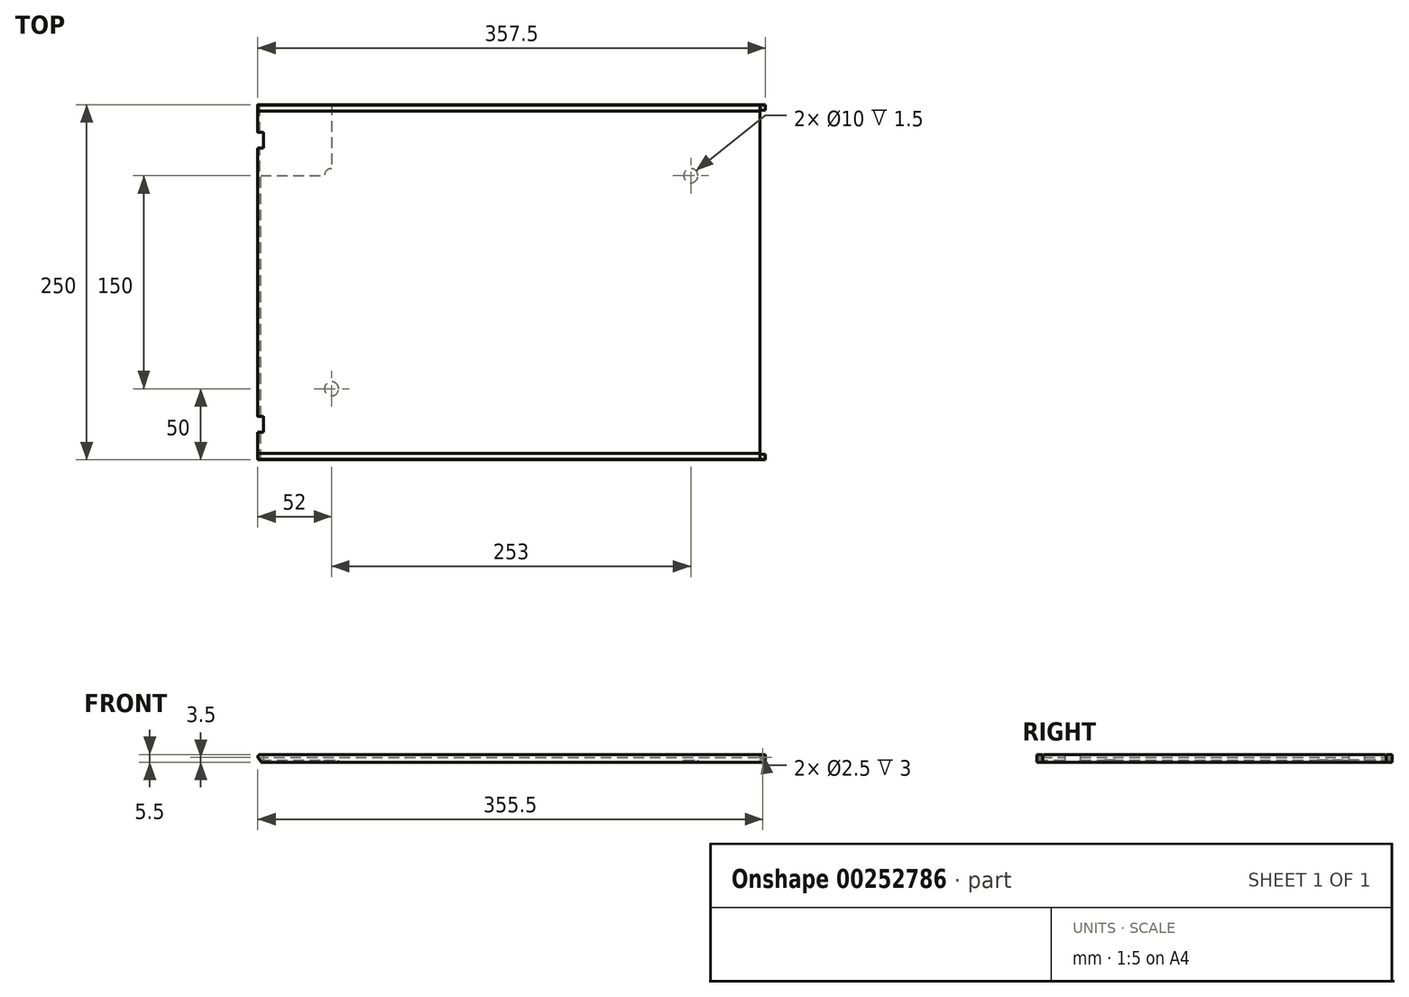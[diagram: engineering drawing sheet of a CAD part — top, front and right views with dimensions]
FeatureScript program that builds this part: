
annotation { "Feature Type Name" : "Feature", "Feature Type Description" : "" }
export const myFeature = defineFeature(function(context is Context, id is Id, definition is map)
    precondition{}
    {
        {
            var Q0;
            Q0=qCreatedBy(makeId("Top.planeOp"),FACE);
            var sketch = newSketch(context, id + "F0", { "sketchPlane" : qUnion([Q0])});
            skLineSegment(sketch, "E0.bottom", {"start": v(-175, -125) * mm, "end": v(175, -125) * mm});
            skLineSegment(sketch, "E0.top", {"start": v(-175, 125) * mm, "end": v(175, 125) * mm});
            skLineSegment(sketch, "E0.left", {"start": v(-175, -125) * mm, "end": v(-175, 125) * mm});
            skLineSegment(sketch, "E0.right", {"start": v(175, -125) * mm, "end": v(175, 125) * mm});
            skPoint(sketch, "E0.middle", {"position": v(0, 0) * mm});
            skSolve(sketch);
        }
        {
            var Q0;
            Q0 = qSketchRegion(id + "F0", true);
            extrude(context, id + "F1", {"entities" : qUnion([Q0]), "endBound" : BoundingType.SYMMETRIC, "depth" : 4 * mm});
        }
        {
            var Q0;
            Q0=makeQuery(id+"F1.opExtrude","SWEPT_FACE",FACE,{"disambiguationData":[OSD([sQuery(id+"F0.wireOp",EDGE,"E0.right")])]});
            var sketch = newSketch(context, id + "F2", { "sketchPlane" : qUnion([Q0])});
            skLineSegment(sketch, "E1.bottom", {"start": v(-125, 2) * mm, "end": v(-121, 2) * mm});
            skLineSegment(sketch, "E1.top", {"start": v(-125, -2) * mm, "end": v(-121, -2) * mm});
            skLineSegment(sketch, "E1.left", {"start": v(-125, 2) * mm, "end": v(-125, -2) * mm});
            skLineSegment(sketch, "E1.right", {"start": v(-121, 2) * mm, "end": v(-121, -2) * mm});
            skLineSegment(sketch, "E2.MirrorCS", {"start": v(125, 2) * mm, "end": v(121, 2) * mm});
            skLineSegment(sketch, "E3.MirrorCS", {"start": v(125, 2) * mm, "end": v(125, -2) * mm});
            skLineSegment(sketch, "E4.MirrorCS", {"start": v(125, -2) * mm, "end": v(121, -2) * mm});
            skLineSegment(sketch, "E5.MirrorCS", {"start": v(121, 2) * mm, "end": v(121, -2) * mm});
            skSolve(sketch);
        }
        {
            var Q0;
            Q0=makeQuery(id+"F2.imprint","IMPRINT",FACE,{"disambiguationData":[TD([[makeQuery(id+"F2.imprint","IMPRINT",EDGE,{"derivedFrom":sQuery(id+"F2.wireOp",EDGE,"E1.bottom")}),-1.0]])]});
            var Q1;
            Q1=makeQuery(id+"F2.imprint","IMPRINT",FACE,{"disambiguationData":[TD([[makeQuery(id+"F2.imprint","IMPRINT",EDGE,{"derivedFrom":sQuery(id+"F2.wireOp",EDGE,"E2.MirrorCS")}),-1.0]])]});
            extrude(context, id + "F3", {"entities" : qUnion([Q0, Q1]), "operationType" : NewBodyOperationType.ADD, "depth" : 4 * mm});
        }
        {
            var Q0;
            Q0=makeQuery(id+"F3.opExtrude","SWEPT_FACE",FACE,{"disambiguationData":[OSD([sQuery(id+"F2.wireOp",EDGE,"E1.right")])]});
            var sketch = newSketch(context, id + "F4", { "sketchPlane" : qUnion([Q0])});
            skCircle(sketch, "E6", {"center": v(-177, 0) * mm, "radius": 1.25 * mm});
            skPoint(sketch, "E6.centerSnap0", {"position": v(-179, 0) * mm});
            skPoint(sketch, "E6.centerSnap1", {"position": v(-177, -2) * mm});
            skSolve(sketch);
        }
        {
            var Q0;
            Q0 = qSketchRegion(id + "F4", true);
            extrude(context, id + "F5", {"entities" : qUnion([Q0]), "operationType" : NewBodyOperationType.REMOVE, "oppositeDirection" : true, "depth" : 3 * mm});
        }
        {
            var Q0;
            Q0=makeQuery(id+"F3.opExtrude","SWEPT_FACE",FACE,{"disambiguationData":[OSD([sQuery(id+"F2.wireOp",EDGE,"E5.MirrorCS")])]});
            var sketch = newSketch(context, id + "F6", { "sketchPlane" : qUnion([Q0])});
            skCircle(sketch, "E7", {"center": v(177, 0) * mm, "radius": 1.25 * mm});
            skPoint(sketch, "E7.centerSnap0", {"position": v(179, 0) * mm});
            skPoint(sketch, "E7.centerSnap1", {"position": v(177, -2) * mm});
            skSolve(sketch);
        }
        {
            var Q0;
            Q0 = qSketchRegion(id + "F6", true);
            extrude(context, id + "F7", {"entities" : qUnion([Q0]), "operationType" : NewBodyOperationType.REMOVE, "oppositeDirection" : true, "depth" : 3 * mm});
        }
        {
            var Q0;
            Q0=makeQuery(id+"F1.opExtrude","SWEPT_FACE",FACE,{"disambiguationData":[OSD([sQuery(id+"F0.wireOp",EDGE,"E0.left")])]});
            var sketch = newSketch(context, id + "F8", { "sketchPlane" : qUnion([Q0])});
            skLineSegment(sketch, "E8.bottom", {"start": v(-5.5, 2) * mm, "end": v(5.5, 2) * mm});
            skLineSegment(sketch, "E8.top", {"start": v(-5.5, -2) * mm, "end": v(5.5, -2) * mm});
            skLineSegment(sketch, "E8.left", {"start": v(-5.5, 2) * mm, "end": v(-5.5, -2) * mm});
            skLineSegment(sketch, "E8.right", {"start": v(5.5, 2) * mm, "end": v(5.5, -2) * mm});
            skPoint(sketch, "E8.middle", {"position": v(0, 0) * mm});
            skLineSegment(sketch, "E9", {"start": v(-125, 0) * mm, "end": v(-100, 0) * mm});
            skPoint(sketch, "E9.endSnap0", {"position": v(-125, 0) * mm});
            skLineSegment(sketch, "E10.bottom", {"start": v(-105.5, 2) * mm, "end": v(-94.5, 2) * mm});
            skLineSegment(sketch, "E10.top", {"start": v(-105.5, -2) * mm, "end": v(-94.5, -2) * mm});
            skLineSegment(sketch, "E10.left", {"start": v(-105.5, 2) * mm, "end": v(-105.5, -2) * mm});
            skLineSegment(sketch, "E10.right", {"start": v(-94.5, 2) * mm, "end": v(-94.5, -2) * mm});
            skPoint(sketch, "E10.middle", {"position": v(-100, 0) * mm});
            skLineSegment(sketch, "E11.MirrorCS", {"start": v(105.5, -2) * mm, "end": v(94.5, -2) * mm});
            skLineSegment(sketch, "E12.MirrorCS", {"start": v(105.5, 2) * mm, "end": v(94.5, 2) * mm});
            skLineSegment(sketch, "E13.MirrorCS", {"start": v(105.5, 2) * mm, "end": v(105.5, -2) * mm});
            skLineSegment(sketch, "E14.MirrorCS", {"start": v(94.5, 2) * mm, "end": v(94.5, -2) * mm});
            skSolve(sketch);
        }
        {
            var Q0;
            {var subQ4=sQuery(id+"F8.wireOp",EDGE,"E10.bottom");Q0=makeQuery(id+"F8.imprint","IMPRINT",FACE,{"disambiguationData":[TD([[makeQuery(id+"F8.imprint","IMPRINT",EDGE,{"derivedFrom":subQ4}),1.0]])]});}
            var Q1;
            Q1=makeQuery(id+"F8.imprint","IMPRINT",FACE,{"disambiguationData":[TD([[makeQuery(id+"F8.imprint","IMPRINT",EDGE,{"derivedFrom":sQuery(id+"F8.wireOp",EDGE,"E11.MirrorCS")}),-1.0]])]});
            extrude(context, id + "F9", {"entities" : qUnion([Q0, Q1]), "operationType" : NewBodyOperationType.REMOVE, "oppositeDirection" : true, "depth" : .5 * mm});
        }
        {
            var Q0;
            Q0=makeQuery(id+"F3.boolean.opBoolean","MERGE",FACE,{"derivedFrom":[makeQuery(id+"F1.opExtrude","SWEPT_FACE",FACE,{"disambiguationData":[OSD([sQuery(id+"F0.wireOp",EDGE,"E0.top")])]}),makeQuery(id+"F3.opExtrude","SWEPT_FACE",FACE,{"disambiguationData":[OSD([sQuery(id+"F2.wireOp",EDGE,"E3.MirrorCS")])]})]});
            var sketch = newSketch(context, id + "F10", { "sketchPlane" : qUnion([Q0])});
            skLineSegment(sketch, "E15", {"start": v(175, 2) * mm, "end": v(176.5, 2) * mm});
            skLineSegment(sketch, "E16", {"start": v(175, -2) * mm, "end": v(176.5, -2) * mm});
            skLineSegment(sketch, "E17", {"start": v(176.5, -2) * mm, "end": v(176.5, 2) * mm});
            skCircle(sketch, "E18", {"center": v(176.5, 0) * mm, "radius": 2 * mm});
            skLineSegment(sketch, "E19", {"start": v(178.5, 0) * mm, "end": v(176.94, -1.95) * mm});
            skSolve(sketch);
        }
        {
            var Q0;
            {var subQ2=sQuery(id+"F0.wireOp",EDGE,"E0.top");var subQ3=makeQuery(id+"F1.opExtrude","SWEPT_EDGE",EDGE,{"disambiguationData":[OSD([subQ2,sQuery(id+"F0.wireOp",EDGE,"E0.left")])]});Q0=makeQuery(id+"F10.imprint","IMPRINT",FACE,{"disambiguationData":[TD([[makeQuery(id+"F10.imprint","IMPRINT",EDGE,{"derivedFrom":subQ3}),1.0]])]});}
            var Q1;
            {var subQ0=sQuery(id+"F10.wireOp",EDGE,"E17");Q1=makeQuery(id+"F10.imprint","IMPRINT",FACE,{"disambiguationData":[TD([[makeQuery(id+"F10.imprint","IMPRINT",EDGE,{"derivedFrom":subQ0}),-1.0]])]});}
            var Q2;
            {var subQ0=sQuery(id+"F10.wireOp",EDGE,"E17");Q2=makeQuery(id+"F10.imprint","IMPRINT",FACE,{"disambiguationData":[TD([[makeQuery(id+"F10.imprint","IMPRINT",EDGE,{"derivedFrom":subQ0}),1.0]])]});}
            extrude(context, id + "F11", {"entities" : qUnion([Q0, Q1, Q2]), "operationType" : NewBodyOperationType.ADD, "oppositeDirection" : true, "depth" : 250 * mm});
        }
        {
            var Q0;
            Q0=makeQuery(id+"F3.boolean.opBoolean","MERGE",FACE,{"derivedFrom":[makeQuery(id+"F1.opExtrude","CAP_FACE",FACE,{"disambiguationData":[OSD([sQuery(id+"F0.wireOp",EDGE,"E0.bottom"),sQuery(id+"F0.wireOp",EDGE,"E0.top"),sQuery(id+"F0.wireOp",EDGE,"E0.left"),sQuery(id+"F0.wireOp",EDGE,"E0.right")])],"isStart":false}),makeQuery(id+"F3.opExtrude","SWEPT_FACE",FACE,{"disambiguationData":[OSD([sQuery(id+"F2.wireOp",EDGE,"E1.bottom")])]}),makeQuery(id+"F3.opExtrude","SWEPT_FACE",FACE,{"disambiguationData":[OSD([sQuery(id+"F2.wireOp",EDGE,"E2.MirrorCS")])]})]});
            var sketch = newSketch(context, id + "F12", { "sketchPlane" : qUnion([Q0])});
            skLineSegment(sketch, "E20", {"start": v(-168.3, 125) * mm, "end": v(-168.3, 124.5) * mm});
            skLineSegment(sketch, "E21.top", {"start": v(-185, 120.4) * mm, "end": v(175, 120.4) * mm});
            skLineSegment(sketch, "E22.MirrorCS", {"start": v(-185, -120.4) * mm, "end": v(175, -120.4) * mm});
            skLineSegment(sketch, "E23", {"start": v(-185, 124.5) * mm, "end": v(-185, 120.4) * mm});
            skLineSegment(sketch, "E24", {"start": v(-185, 124.5) * mm, "end": v(175, 124.5) * mm});
            skLineSegment(sketch, "E25", {"start": v(175, 120.4) * mm, "end": v(175, 124.5) * mm});
            skLineSegment(sketch, "E26.MirrorCS", {"start": v(175, -120.4) * mm, "end": v(175, -124.5) * mm});
            skLineSegment(sketch, "E27.MirrorCS", {"start": v(-185, -124.5) * mm, "end": v(175, -124.5) * mm});
            skLineSegment(sketch, "E28.MirrorCS", {"start": v(-185, -124.5) * mm, "end": v(-185, -120.4) * mm});
            skSolve(sketch);
        }
        {
            var Q0;
            {var subQ0=sQuery(id+"F12.wireOp",EDGE,"E26.MirrorCS");var subQ3=sQuery(id+"F12.wireOp",EDGE,"E27.MirrorCS");var subQ4=makeQuery(id+"F12.imprint","INTERSECT",VERTEX,{"derivedFrom":[subQ0,subQ3]});Q0=makeQuery(id+"F12.imprint","IMPRINT",FACE,{"disambiguationData":[TD([[makeQuery(id+"F12.imprint","IMPRINT",EDGE,{"disambiguationData":[TD([[subQ4,1.0]])],"derivedFrom":subQ3}),1.0]])]});}
            var Q1;
            {var subQ0=sQuery(id+"F12.wireOp",EDGE,"E28.MirrorCS");Q1=makeQuery(id+"F12.imprint","IMPRINT",FACE,{"disambiguationData":[TD([[makeQuery(id+"F12.imprint","IMPRINT",EDGE,{"derivedFrom":subQ0}),-1.0]])]});}
            var Q2;
            {var subQ3=sQuery(id+"F12.wireOp",EDGE,"E24");var subQ5=makeQuery(id+"F12.imprint","INTERSECT",VERTEX,{"derivedFrom":[sQuery(id+"F12.wireOp",EDGE,"E20"),subQ3]});Q2=makeQuery(id+"F12.imprint","IMPRINT",FACE,{"disambiguationData":[TD([[makeQuery(id+"F12.imprint","IMPRINT",EDGE,{"disambiguationData":[TD([[subQ5,1.0]])],"derivedFrom":subQ3}),-1.0]])]});}
            var Q3;
            {var subQ0=sQuery(id+"F12.wireOp",EDGE,"E23");Q3=makeQuery(id+"F12.imprint","IMPRINT",FACE,{"disambiguationData":[TD([[makeQuery(id+"F12.imprint","IMPRINT",EDGE,{"derivedFrom":subQ0}),1.0]])]});}
            extrude(context, id + "F13", {"entities" : qUnion([Q0, Q1, Q2, Q3]), "operationType" : NewBodyOperationType.REMOVE, "oppositeDirection" : true, "depth" : 2 * mm});
        }
        {
            var Q0;
            Q0=makeQuery(id+"F13.boolean.opBoolean","COPY",EDGE,{"derivedFrom":makeQuery(id+"F13.opExtrude","CAP_EDGE",EDGE,{"disambiguationData":[OSD([sQuery(id+"F12.wireOp",EDGE,"E22.MirrorCS")])],"isStart":false})});
            var Q1;
            Q1=makeQuery(id+"F13.boolean.opBoolean","COPY",EDGE,{"derivedFrom":makeQuery(id+"F13.opExtrude","CAP_EDGE",EDGE,{"disambiguationData":[OSD([sQuery(id+"F12.wireOp",EDGE,"44075e42-1595-40cc-9fb6-60341f8f37b10.MirrorCS")])],"isStart":false})});
            var Q2;
            Q2=makeQuery(id+"F13.boolean.opBoolean","COPY",EDGE,{"derivedFrom":makeQuery(id+"F13.opExtrude","CAP_EDGE",EDGE,{"disambiguationData":[OSD([sQuery(id+"F12.wireOp",EDGE,"E21.top")])],"isStart":false})});
            var Q3;
            Q3=makeQuery(id+"F13.boolean.opBoolean","COPY",EDGE,{"derivedFrom":makeQuery(id+"F13.opExtrude","CAP_EDGE",EDGE,{"disambiguationData":[OSD([sQuery(id+"F12.wireOp",EDGE,"E21.bottom")])],"isStart":false})});
            var Q4;
            Q4=makeQuery(id+"F13.boolean.opBoolean","COPY",EDGE,{"derivedFrom":makeQuery(id+"F13.opExtrude","CAP_EDGE",EDGE,{"disambiguationData":[OSD([sQuery(id+"F12.wireOp",EDGE,"E24")])],"isStart":false})});
            var Q5;
            Q5=makeQuery(id+"F13.boolean.opBoolean","COPY",EDGE,{"derivedFrom":makeQuery(id+"F13.opExtrude","CAP_EDGE",EDGE,{"disambiguationData":[OSD([sQuery(id+"F12.wireOp",EDGE,"E27.MirrorCS")])],"isStart":false})});
            fillet(context, id + "F14", {"entities" : qUnion([Q0, Q1, Q2, Q3, Q4, Q5]), "radius" : 1.5 * mm, "tangentPropagation" : true, "allowEdgeOverflow" : false});
        }
        {
            var Q0;
            {var subQ4=sQuery(id+"F8.wireOp",EDGE,"E10.bottom");Q0=makeQuery(id+"F8.imprint","IMPRINT",FACE,{"disambiguationData":[TD([[makeQuery(id+"F8.imprint","IMPRINT",EDGE,{"derivedFrom":subQ4}),1.0]])]});}
            var Q1;
            Q1=makeQuery(id+"F8.imprint","IMPRINT",FACE,{"disambiguationData":[TD([[makeQuery(id+"F8.imprint","IMPRINT",EDGE,{"derivedFrom":sQuery(id+"F8.wireOp",EDGE,"E11.MirrorCS")}),-1.0]])]});
            extrude(context, id + "F15", {"entities" : qUnion([Q0, Q1]), "operationType" : NewBodyOperationType.REMOVE, "depth" : 25 * mm});
        }
        {
            var Q0;
            Q0=makeQuery(id+"F11.boolean.opBoolean","MERGE",FACE,{"derivedFrom":[makeQuery(id+"F3.boolean.opBoolean","MERGE",FACE,{"derivedFrom":[makeQuery(id+"F1.opExtrude","CAP_FACE",FACE,{"disambiguationData":[OSD([sQuery(id+"F0.wireOp",EDGE,"E0.bottom"),sQuery(id+"F0.wireOp",EDGE,"E0.top"),sQuery(id+"F0.wireOp",EDGE,"E0.left"),sQuery(id+"F0.wireOp",EDGE,"E0.right")])],"isStart":true}),makeQuery(id+"F3.opExtrude","SWEPT_FACE",FACE,{"disambiguationData":[OSD([sQuery(id+"F2.wireOp",EDGE,"E1.top")])]}),makeQuery(id+"F3.opExtrude","SWEPT_FACE",FACE,{"disambiguationData":[OSD([sQuery(id+"F2.wireOp",EDGE,"E4.MirrorCS")])]})]}),makeQuery(id+"F11.opExtrude","SWEPT_FACE",FACE,{"disambiguationData":[OSD([sQuery(id+"F10.wireOp",EDGE,"E16")])]})]});
            var sketch = newSketch(context, id + "F16", { "sketchPlane" : qUnion([Q0])});
            skLineSegment(sketch, "E29.bottom", {"start": v(-176.5, -125) * mm, "end": v(-126.5, -125) * mm});
            skLineSegment(sketch, "E29.top", {"start": v(-176.5, -75) * mm, "end": v(-126.5, -75) * mm});
            skLineSegment(sketch, "E29.left", {"start": v(-176.5, -125) * mm, "end": v(-176.5, -75) * mm});
            skLineSegment(sketch, "E29.right", {"start": v(-126.5, -125) * mm, "end": v(-126.5, -75) * mm});
            skCircle(sketch, "E30", {"center": v(-126.5, -75) * mm, "radius": 5 * mm});
            skCircle(sketch, "E31.MirrorC", {"center": v(-126.5, 75) * mm, "radius": 5 * mm});
            skCircle(sketch, "E32.MirrorC", {"center": v(126.5, 75) * mm, "radius": 5 * mm});
            skCircle(sketch, "E33.MirrorC", {"center": v(126.5, -75) * mm, "radius": 5 * mm});
            skSolve(sketch);
        }
        {
            var Q0;
            {var subQ0=sQuery(id+"F16.wireOp",EDGE,"E29.right");var subQ1=sQuery(id+"F16.wireOp",EDGE,"E29.top");var subQ2=makeQuery(id+"F16.imprint","INTERSECT",VERTEX,{"derivedFrom":[subQ1,subQ0]});Q0=makeQuery(id+"F16.imprint","IMPRINT",FACE,{"disambiguationData":[TD([[makeQuery(id+"F16.imprint","IMPRINT",EDGE,{"disambiguationData":[TD([[subQ2,1.0]])],"derivedFrom":subQ1}),-1.0]])]});}
            var Q1;
            {var subQ0=sQuery(id+"F16.wireOp",EDGE,"E29.right");var subQ1=sQuery(id+"F16.wireOp",EDGE,"E29.top");var subQ2=makeQuery(id+"F16.imprint","INTERSECT",VERTEX,{"derivedFrom":[subQ1,subQ0]});Q1=makeQuery(id+"F16.imprint","IMPRINT",FACE,{"disambiguationData":[TD([[makeQuery(id+"F16.imprint","IMPRINT",EDGE,{"disambiguationData":[TD([[subQ2,1.0]])],"derivedFrom":subQ1}),1.0]])]});}
            var Q2;
            Q2=makeQuery(id+"F16.imprint","IMPRINT",FACE,{"disambiguationData":[TD([[makeQuery(id+"F16.imprint","IMPRINT",EDGE,{"derivedFrom":sQuery(id+"F16.wireOp",EDGE,"E31.MirrorC")}),-1.0]])]});
            var Q3;
            Q3=makeQuery(id+"F16.imprint","IMPRINT",FACE,{"disambiguationData":[TD([[makeQuery(id+"F16.imprint","IMPRINT",EDGE,{"derivedFrom":sQuery(id+"F16.wireOp",EDGE,"E33.MirrorC")}),-1.0]])]});
            var Q4;
            Q4=makeQuery(id+"F16.imprint","IMPRINT",FACE,{"disambiguationData":[TD([[makeQuery(id+"F16.imprint","IMPRINT",EDGE,{"derivedFrom":sQuery(id+"F16.wireOp",EDGE,"E32.MirrorC")}),1.0]])]});
            extrude(context, id + "F17", {"entities" : qUnion([Q0, Q1, Q2, Q3, Q4]), "operationType" : NewBodyOperationType.ADD, "depth" : 1.5 * mm});
        }
    });
